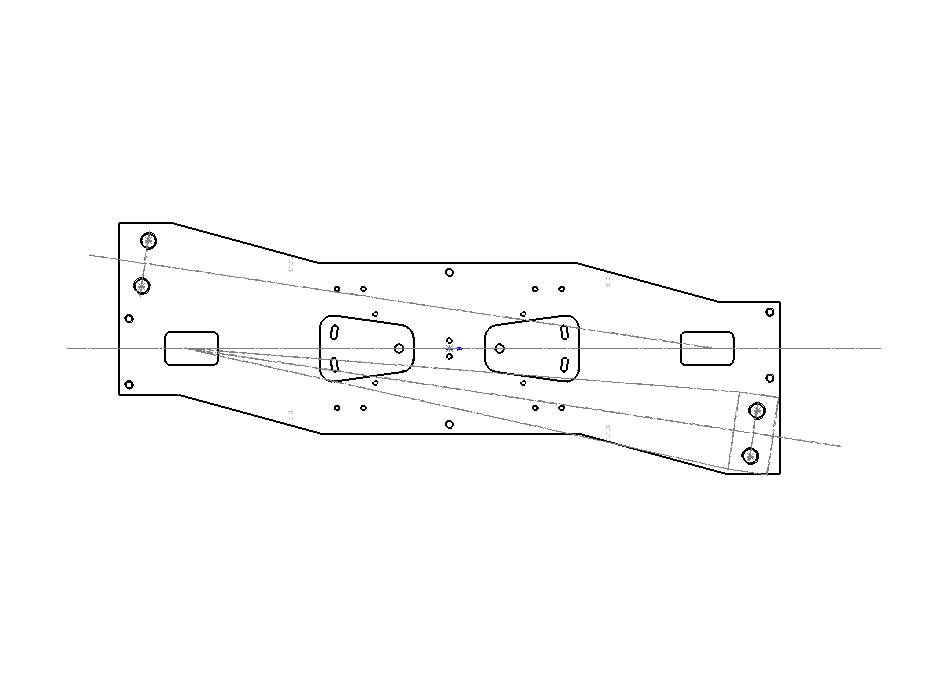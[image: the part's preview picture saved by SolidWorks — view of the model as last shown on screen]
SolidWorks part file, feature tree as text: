
SOLIDWORKS PART (.sldprt)
format: sldprt  version: not decoded by parser v0  size: 2,164,224 bytes
history: native  units: mm
features: sketch x27, thread x25, hole x10, cut_extrude x4, plane x4, extrude x2, material x1 (+12 scaffold rows collapsed)
feature tree (85):
  scaffold x12  (default folders/planes/origin — collapsed)
  material  "Material <not specified>"
  sketch  "Sketch1"  dims[D1=16.0mm D2=500.0mm D3=250.0mm]
  extrude  "Base-Extrude"  Depth=130mm
  sketch  "Sketch3"  dims[c1.D1=10.0mm c1.D2=40.0mm c1.D3=40.0mm c1.D4=10.0mm c2.D1=160.0mm c2.D4=160.0mm c2.D5=110.0mm c2.D6=110.0mm]
  extrude  "Extrusion for Blade Clamping"  [1 undecoded]
  sketch  "Sketch4"  dims[c1.D1=10.0mm c1.D2=55.0mm c1.D3=10.0mm c1.D4=45.0mm c2.D1=130.0mm c2.D3=130.0mm c2.D5=~43.501561mm c2.D4=~54.083269mm c3.D5=45.0mm c3.D6=45.0mm c4.D5=45.0mm c4.D6=45.0mm c5.D5=45.0mm c5.D6=45.0mm c6.D5=45.0mm c6.D6=45.0mm c7.D5=45.0mm c7.D6=45.0mm c8.D5=45.0mm c8.D6=45.0mm c9.D5=45.0mm c9.D6=45.0mm c10.D5=45.0mm c10.D6=45.0mm c11.D5=45.0mm c11.D6=45.0mm c12.D5=45.0mm c12.D6=45.0mm c13.D5=45.0mm c13.D6=45.0mm c14.D5=45.0mm c14.D6=45.0mm c15.D5=45.0mm c15.D6=45.0mm c16.D5=45.0mm c16.D6=45.0mm c17.D5=45.0mm c17.D6=45.0mm c17.D4=45.0mm c18.D5=110.0mm c18.D6=55.0mm c18.D2=~62.64982mm c19.D6=55.0mm c19.D7=55.0mm c20.D6=55.0mm c20.D7=55.0mm c21.D6=55.0mm c21.D7=55.0mm c22.D6=55.0mm c22.D7=55.0mm c23.D6=55.0mm c23.D7=55.0mm c24.D6=55.0mm c24.D7=55.0mm c25.D6=55.0mm c25.D7=55.0mm c26.D6=55.0mm c26.D7=55.0mm c27.D6=55.0mm c27.D7=55.0mm c28.D6=55.0mm c28.D7=55.0mm c28.D2=45.0mm c29.D6=110.0mm]
  cut_extrude  "Cutaway to Balance Blade Extrusion"  [1 undecoded]
  sketch  "Sketch5"  dims[D2=4.0mm D1=200.0mm D3=25.0mm D4=25.0mm D5=15.0mm]
  cut_extrude  "Holes for Wires from Blades"  [1 undecoded]
  sketch  "Sketch7"  dims[c1.D12=10.0mm c1.D11=10.0mm c1.D1=220.0mm c1.D2=30.0mm c1.D3=15.0mm c2.D1=50.0mm c2.D2=15.0mm c2.D3=42.0mm c2.D4=90.0mm c3.D1=25.0mm c3.D2=35.0mm c3.D3=71.0mm c3.D5=10.0mm c3.D6=88.0mm c3.D7=73.0mm c3.D8=10.0mm c3.D9=50.0mm c3.D10=25.0mm c4.D2=50.0mm c4.D11=25.0mm c4.D9=25.0mm c4.D10=25.0mm c5.D2=25.0mm c5.D11=25.0mm c5.D4=10.0mm c5.D5=30.0mm c5.D8=~52.642346mm c6.D8=15.0deg c6.D9=30.0mm c6.D2=88.0mm c6.D4=~53.96792mm c7.D4=15.0deg c7.D7=71.0mm c7.D10=~51.440077mm c8.D10=7.5deg c8.D8=~51.440077mm c9.D8=8.0deg c9.D10=~535.34499mm c10.D10=8.0deg c10.D4=~52.742707mm c11.D4=8.0deg c11.D10=~51.514975mm c12.D10=8.0deg c12.D11=51.0mm]
  cut_extrude  "Milling for UpperWire Pitch Adjustment"  Depth=5mm
  sketch  "Sketch9"  dims[c1.D2=~6.012457mm c1.D1=220.0mm c1.D4=3.0mm c1.D5=113.0mm c1.D6=6.0mm c1.D7=6.0mm c2.D6=3.0mm c2.D7=107.0mm c2.D10=3.0mm c2.D5=3.0mm c2.D4=3.0mm c3.D5=~107.002847mm c3.D1=90.0mm c4.D5=87.0mm c4.D6=107.0mm c4.D7=87.0mm c4.D4=113.0mm c4.D9=93.0mm c4.D10=9.5mm c5.D6=113.0mm c5.D1=6.35mm c5.D4=3.0mm c6.D6=~2.15265mm c6.D7=3.0mm c6.D10=3.0mm c6.D5=88.0mm c6.D4=~87.884838mm c6.D1=110.0mm c6.D2=110.0mm c7.D2=10.0deg c7.D3=110.0mm c8.D3=6.0deg c8.D8=110.0mm c9.D8=4.0deg c9.D6=110.0mm c9.D7=110.0mm c10.D7=11.0deg c10.D9=~520.81731mm c11.D9=15.0deg c11.D11=110.0mm c12.D11=4.0deg c12.D5=~109.732046mm c12.D9=~520.81731mm c13.D9=11.0deg c13.D4=~122.230557mm c14.D4=4.0deg c15.D4=~122.230557mm c16.D4=10.0deg c16.D8=~71.905831mm c17.D8=9.5deg c17.D11=60.0mm c17.D12=110.0mm c18.D12=6.0deg c18.D13=~6.003745mm c18.D8=38.0mm c19.D13=110.0mm c19.D10=~121.611079mm c20.D10=10.0deg c20.D11=90.0mm c21.D11=6.0deg c21.D4=4.3053mm c21.D3=5.0mm]
  cut_extrude  "Slots/Hole for UpperWire Pitch Adj"  [1 undecoded]
  sketch  "Sketch10"  dims[c1.D8=2.0mm c1.D9=2.0mm c1.D1=~501.490328mm c2.D1=8.5deg c2.D2=477.7536mm c3.D2=8.5deg c3.D3=200.0mm c3.D4=200.0mm c3.D5=435.0mm c3.D6=435.0mm c3.D7=34.595mm c3.D10=34.595mm c3.D11=15.0mm c3.D12=30.0mm c3.D13=12.2mm c3.D14=59.0mm c3.D15=~0.692676mm c3.D9=34.595mm c4.D7=34.595mm]
  hole  "#8-32 Tapped Hole1"  Diameter=3.4544mm Depth=16.00005mm
  sketch  "3DSketch1"  dims[c1.D1=~12.229099mm c1.D3=10.0mm c1.D2=~3.068077mm c2.D1=12.0mm c2.D2=6.0mm]
  sketch  "Sketch12"  dims[hole-wizard template sketch: 60 standard entries collapsed; hole parameters kept: c18.Thru Tap Drill Depth=~16.00005mm]
  thread  "Cosmetic Thread1"  Diameter=4.1656mm  [1 undecoded]
  thread  "Cosmetic Thread2"  Diameter=4.1656mm  [1 undecoded]
  hole  "1/4-20 Tapped Hole1"  [1 undecoded]
  sketch  "Sketch14"  dims[D1=7.5mm D2=7.5mm D3=50.0mm D4=7.5mm D5=7.5mm D6=50.0mm]
  thread  "Cosmetic Thread3"  Diameter=12.7mm  [1 undecoded]
  thread  "Cosmetic Thread4"  Diameter=12.7mm  [1 undecoded]
  thread  "Cosmetic Thread5"  Diameter=12.7mm  [1 undecoded]
  thread  "Cosmetic Thread6"  Diameter=12.7mm  [1 undecoded]
  thread  "Cosmetic Thread7"  Diameter=12.7mm  [1 undecoded]
  sketch  "Sketch13"  dims[hole-wizard template sketch: 60 standard entries collapsed; hole parameters kept: c18.Thru Tap Drill Depth=~16.00005mm]
  hole  "#8-32 Tapped Hole2"  Diameter=3.4544mm Depth=16.00005mm
  sketch  "Sketch16"  dims[D1=15.0mm D2=20.0mm D3=20.0mm D4=20.0mm D5=10.0mm D6=20.0mm D7=10.0mm D8=20.0mm D9=15.0mm D10=20.0mm D11=20.0mm]
  sketch  "Sketch15"  dims[hole-wizard template sketch: 60 standard entries collapsed; hole parameters kept: c18.Thru Tap Drill Depth=~16.00005mm]
  thread  "Cosmetic Thread8"  Diameter=8.3312mm  [1 undecoded]
  thread  "Cosmetic Thread9"  Diameter=8.3312mm  [1 undecoded]
  thread  "Cosmetic Thread10"  Diameter=8.3312mm  [1 undecoded]
  thread  "Cosmetic Thread11"  Diameter=8.3312mm  [1 undecoded]
  thread  "Cosmetic Thread12"  Diameter=8.3312mm  [1 undecoded]
  thread  "Cosmetic Thread13"  Diameter=8.3312mm  [1 undecoded]
  thread  "Cosmetic Thread14"  Diameter=8.3312mm  [1 undecoded]
  thread  "Cosmetic Thread15"  Diameter=8.3312mm  [1 undecoded]
  hole  "#8-32 Tapped Hole3"  Diameter=3.4544mm Depth=16.00005mm
  sketch  "Sketch18"  dims[D1=26.0mm D2=56.0mm]
  sketch  "Sketch17"  dims[hole-wizard template sketch: 60 standard entries collapsed; hole parameters kept: c18.Thru Tap Drill Depth=~16.00005mm]
  thread  "Cosmetic Thread16"  Diameter=8.3312mm  [1 undecoded]
  thread  "Cosmetic Thread17"  Diameter=8.3312mm  [1 undecoded]
  thread  "Cosmetic Thread18"  Diameter=8.3312mm  [1 undecoded]
  thread  "Cosmetic Thread19"  Diameter=8.3312mm  [1 undecoded]
  hole  "1/4-20 Tapped Hole2"  Diameter=5.1054mm Depth=16.00005mm
  sketch  "Sketch20"  dims[D1=7.5mm D2=7.5mm]
  sketch  "Sketch19"  dims[hole-wizard template sketch: 60 standard entries collapsed; hole parameters kept: c18.Thru Tap Drill Depth=~16.00005mm]
  thread  "Cosmetic Thread20"  Diameter=6.35mm  [1 undecoded]
  thread  "Cosmetic Thread21"  Diameter=6.35mm  [1 undecoded]
  plane  "Plane1"  Offset=24.7mm
  hole  "#8-32 Tapped Hole5"  Diameter=3.4544mm Depth=12.2936mm
  sketch  "Sketch22"  dims[D1=130.0mm D2=8.0mm]
  sketch  "Sketch21"  dims[hole-wizard template sketch: 47 standard entries collapsed; hole parameters kept: c15.Tap Drill Depth=12.2936mm c15.D3=~14.816244mm c15.Drill Angle=118.0deg]
  plane  "Plane2"  Offset=24mm
  hole  "#8-32 Tapped Hole6"  Diameter=3.4544mm Depth=12.2936mm
  sketch  "Sketch24"  dims[D1=8.0mm D2=130.0mm]
  sketch  "Sketch23"  dims[hole-wizard template sketch: 47 standard entries collapsed; hole parameters kept: c15.Tap Drill Depth=12.2936mm c15.D3=~14.816244mm c15.Drill Angle=118.0deg]
  plane  "Plane3"  Offset=24.7mm
  hole  "#8-32 Tapped Hole7"  Diameter=3.4544mm Depth=12.2936mm
  sketch  "Sketch26"
  sketch  "Sketch25"  dims[hole-wizard template sketch: 47 standard entries collapsed; hole parameters kept: c15.Tap Drill Depth=12.2936mm c15.D3=~14.816244mm c15.Drill Angle=118.0deg]
  plane  "Plane4"  Offset=24mm
  hole  "#8-32 Tapped Hole8"  Diameter=3.4544mm Depth=12.2936mm
  sketch  "Sketch28"
  sketch  "Sketch27"  dims[hole-wizard template sketch: 47 standard entries collapsed; hole parameters kept: c15.Tap Drill Depth=12.2936mm c15.D3=~14.816244mm c15.Drill Angle=118.0deg]
  hole  "1/2-13 Tapped Hole4"  Diameter=10.71626mm Depth=16.00005mm
  sketch  "3DSketch3"
  sketch  "Sketch30"  dims[hole-wizard template sketch: 60 standard entries collapsed; hole parameters kept: c18.Thru Tap Drill Depth=~16.00005mm]
  thread  "Cosmetic Thread22"  Diameter=12.7mm  [1 undecoded]
  thread  "Cosmetic Thread23"  Diameter=12.7mm  [1 undecoded]
  thread  "Cosmetic Thread24"  Diameter=12.7mm  [1 undecoded]
  thread  "Cosmetic Thread25"  Diameter=12.7mm  [1 undecoded]
decode coverage: 60 of 68 modeling features carry decoded parameters
note: ~ marks probable driven/reference dimensions
note: 30 parameter values undecoded
summary: Diameter pulled from absorbed wizard sketch | no parameter record found for 5 features
note: suppression state not decoded; provenance and decode notes live in map.json
